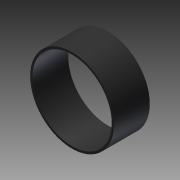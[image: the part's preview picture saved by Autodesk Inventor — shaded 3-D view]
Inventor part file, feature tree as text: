
AUTODESK INVENTOR PART (.ipt)
format: ipt  version: 2014 SP1 (Build 180222100, 222)  size: 82,432 bytes
history: native  units: in
note: dims shown in document units (in); Inventor stores cm internally (conversion verified against a paired STEP export)
features: extrude x1, sketch x1
ambient origin geometry x8: Origin, YZ Plane, XZ Plane, XY Plane, X Axis, Y Axis, Z Axis, Center Point
bodies: Solid1 (feature_tree)
feature tree (2):
  extrude  "Extrusion1"  Depth=0.75in
  sketch  "Sketch1"  dims[d0=1.66in d1=1.75in d2=0.75in d3=0.0in]
